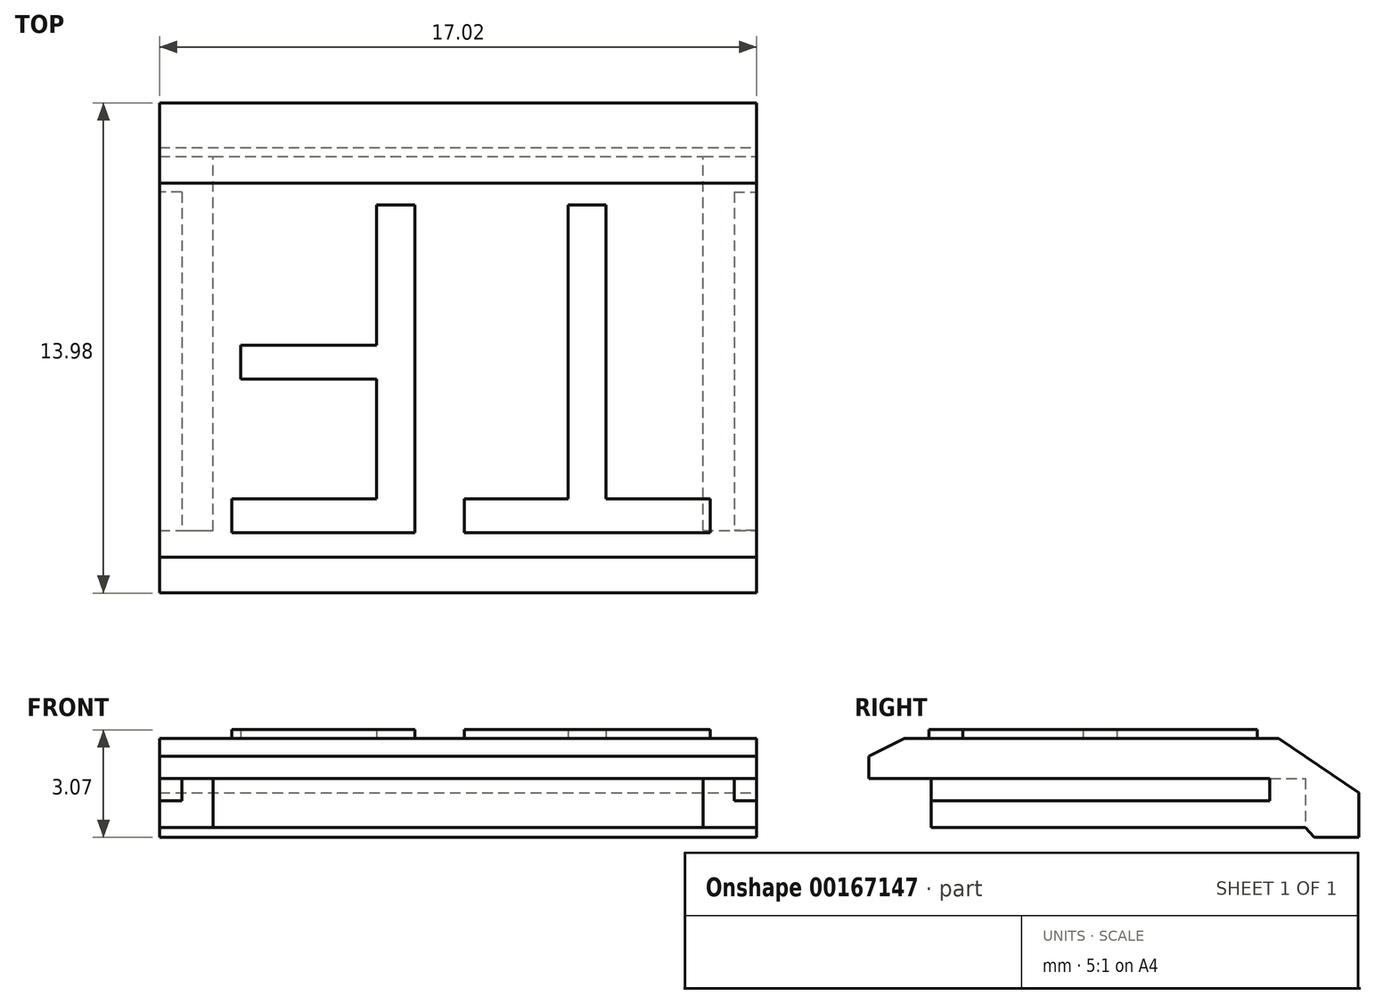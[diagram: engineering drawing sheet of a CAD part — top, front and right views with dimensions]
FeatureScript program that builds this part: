
annotation { "Feature Type Name" : "Feature", "Feature Type Description" : "" }
export const myFeature = defineFeature(function(context is Context, id is Id, definition is map)
    precondition{}
    {
        {
            var Q0;
            Q0=qCreatedBy(makeId("Top.planeOp"),FACE);
            var sketch = newSketch(context, id + "F0", { "sketchPlane" : qUnion([Q0])});
            skLineSegment(sketch, "E0.bottom", {"start": v(-8.5, 6.99) * mm, "end": v(8.5, 6.99) * mm});
            skLineSegment(sketch, "E0.top", {"start": v(-8.5, -6.99) * mm, "end": v(8.5, -6.99) * mm});
            skLineSegment(sketch, "E0.left", {"start": v(-8.5, 6.99) * mm, "end": v(-8.5, -6.99) * mm});
            skLineSegment(sketch, "E0.right", {"start": v(8.5, 6.99) * mm, "end": v(8.5, -6.99) * mm});
            skLineSegment(sketch, "E1", {"start": v(0, 0) * mm, "end": v(0, 6.99) * mm, "construction": true});
            skLineSegment(sketch, "E2", {"start": v(0, 0) * mm, "end": v(-8.5, 0) * mm, "construction": true});
            skSolve(sketch);
        }
        {
            var Q0;
            Q0=makeQuery(id+"F0.imprint","IMPRINT",FACE,{"disambiguationData":[TD([[makeQuery(id+"F0.imprint","IMPRINT",EDGE,{"derivedFrom":sQuery(id+"F0.wireOp",EDGE,"E0.bottom")}),-1.0]])]});
            extrude(context, id + "F1", {"entities" : qUnion([Q0]), "depth" : 2.54 * mm});
        }
        {
            var Q0;
            Q0=makeQuery(id+"F1.opExtrude","SWEPT_FACE",FACE,{"disambiguationData":[OSD([sQuery(id+"F0.wireOp",EDGE,"E0.right")])]});
            var sketch = newSketch(context, id + "F2", { "sketchPlane" : qUnion([Q0])});
            skLineSegment(sketch, "E3", {"start": v(6.99, 0) * mm, "end": v(6.99, -0.28) * mm});
            skLineSegment(sketch, "E4", {"start": v(6.99, -0.28) * mm, "end": v(5.72, -0.28) * mm});
            skLineSegment(sketch, "E5", {"start": v(5.72, -0.28) * mm, "end": v(5.46, 0) * mm});
            skSolve(sketch);
        }
        {
            var Q0;
            {var subQ0=sQuery(id+"F2.wireOp",EDGE,"E3");Q0=makeQuery(id+"F2.imprint","IMPRINT",FACE,{"disambiguationData":[TD([[makeQuery(id+"F2.imprint","IMPRINT",EDGE,{"derivedFrom":subQ0}),-1.0]])]});}
            var Q1;
            Q1=makeQuery(id+"F1.opExtrude","SWEPT_FACE",FACE,{"disambiguationData":[OSD([sQuery(id+"F0.wireOp",EDGE,"E0.left")])]});
            extrude(context, id + "F3", {"entities" : qUnion([Q0]), "operationType" : NewBodyOperationType.ADD, "endBound" : BoundingType.UP_TO_SURFACE, "oppositeDirection" : true, "endBoundEntityFace" : qUnion([Q1]), "depth" : 25.4 * mm});
        }
        {
            var Q0;
            {var subQ0=sQuery(id+"F0.wireOp",EDGE,"E0.right");Q0=makeQuery(id+"F3.boolean.opBoolean","MERGE",FACE,{"derivedFrom":[makeQuery(id+"F1.opExtrude","SWEPT_FACE",FACE,{"disambiguationData":[OSD([subQ0])]}),makeQuery(id+"F3.opExtrude","CAP_FACE",FACE,{"disambiguationData":[OSD([subQ0,sQuery(id+"F2.wireOp",EDGE,"E3"),sQuery(id+"F2.wireOp",EDGE,"E4"),sQuery(id+"F2.wireOp",EDGE,"E5")])],"isStart":true})]});}
            var sketch = newSketch(context, id + "F4", { "sketchPlane" : qUnion([Q0])});
            skLineSegment(sketch, "E6", {"start": v(4.7, 2.54) * mm, "end": v(6.99, 1) * mm});
            skSolve(sketch);
        }
        {
            var Q0;
            {var subQ0=sQuery(id+"F4.wireOp",EDGE,"E6");Q0=makeQuery(id+"F4.imprint","IMPRINT",FACE,{"disambiguationData":[TD([[makeQuery(id+"F4.imprint","IMPRINT",EDGE,{"derivedFrom":subQ0}),1.0]])]});}
            var Q1;
            {var subQ0=sQuery(id+"F0.wireOp",EDGE,"E0.left");Q1=makeQuery(id+"F3.boolean.opBoolean","MERGE",FACE,{"derivedFrom":[makeQuery(id+"F1.opExtrude","SWEPT_FACE",FACE,{"disambiguationData":[OSD([subQ0])]}),makeQuery(id+"F3.opExtrude","CAP_FACE",FACE,{"disambiguationData":[OSD([subQ0])],"isStart":false})]});}
            extrude(context, id + "F5", {"entities" : qUnion([Q0]), "operationType" : NewBodyOperationType.REMOVE, "endBound" : BoundingType.UP_TO_SURFACE, "oppositeDirection" : true, "endBoundEntityFace" : qUnion([Q1]), "depth" : 25.4 * mm});
        }
        {
            var Q0;
            Q0=makeQuery(id+"F1.opExtrude","SWEPT_FACE",FACE,{"disambiguationData":[OSD([sQuery(id+"F0.wireOp",EDGE,"E0.top")])]});
            var sketch = newSketch(context, id + "F6", { "sketchPlane" : qUnion([Q0])});
            skLineSegment(sketch, "E7.bottom", {"start": v(7.87, 1.4) * mm, "end": v(8.5, 1.4) * mm});
            skLineSegment(sketch, "E7.top", {"start": v(7.87, 0.76) * mm, "end": v(8.5, 0.76) * mm});
            skLineSegment(sketch, "E7.left", {"start": v(7.87, 1.4) * mm, "end": v(7.87, 0.76) * mm});
            skLineSegment(sketch, "E7.right", {"start": v(8.5, 1.4) * mm, "end": v(8.5, 0.76) * mm});
            skLineSegment(sketch, "E8", {"start": v(0, 0) * mm, "end": v(0, 2.54) * mm, "construction": true});
            skLineSegment(sketch, "E9.MirrorCS", {"start": v(-7.87, 0.76) * mm, "end": v(-8.5, 0.76) * mm});
            skLineSegment(sketch, "E10.MirrorCS", {"start": v(-7.87, 1.4) * mm, "end": v(-7.87, 0.76) * mm});
            skLineSegment(sketch, "E11.MirrorCS", {"start": v(-7.87, 1.4) * mm, "end": v(-8.5, 1.4) * mm});
            skLineSegment(sketch, "E12.MirrorCS", {"start": v(-8.5, 1.4) * mm, "end": v(-8.5, 0.76) * mm});
            skSolve(sketch);
        }
        {
            var Q0;
            Q0=makeQuery(id+"F6.imprint","IMPRINT",FACE,{"disambiguationData":[TD([[makeQuery(id+"F6.imprint","IMPRINT",EDGE,{"derivedFrom":sQuery(id+"F6.wireOp",EDGE,"E9.MirrorCS")}),-1.0]])]});
            var Q1;
            Q1=makeQuery(id+"F6.imprint","IMPRINT",FACE,{"disambiguationData":[TD([[makeQuery(id+"F6.imprint","IMPRINT",EDGE,{"derivedFrom":sQuery(id+"F6.wireOp",EDGE,"E7.bottom")}),-1.0]])]});
            extrude(context, id + "F7", {"entities" : qUnion([Q0, Q1]), "operationType" : NewBodyOperationType.REMOVE, "oppositeDirection" : true, "depth" : 11.43 * mm});
        }
        {
            var Q0;
            {var subQ0=sQuery(id+"F0.wireOp",EDGE,"E0.right");Q0=makeQuery(id+"F3.boolean.opBoolean","MERGE",FACE,{"derivedFrom":[makeQuery(id+"F1.opExtrude","SWEPT_FACE",FACE,{"disambiguationData":[OSD([subQ0])]}),makeQuery(id+"F3.opExtrude","CAP_FACE",FACE,{"disambiguationData":[OSD([subQ0,sQuery(id+"F2.wireOp",EDGE,"E3"),sQuery(id+"F2.wireOp",EDGE,"E4"),sQuery(id+"F2.wireOp",EDGE,"E5")])],"isStart":true})]});}
            var sketch = newSketch(context, id + "F8", { "sketchPlane" : qUnion([Q0])});
            skLineSegment(sketch, "E13.bottom", {"start": v(-6.98, 1.4) * mm, "end": v(-5.2, 1.4) * mm});
            skLineSegment(sketch, "E13.top", {"start": v(-6.98, 0) * mm, "end": v(-5.2, 0) * mm});
            skLineSegment(sketch, "E13.left", {"start": v(-6.98, 1.4) * mm, "end": v(-6.98, 0) * mm});
            skLineSegment(sketch, "E13.right", {"start": v(-5.2, 1.4) * mm, "end": v(-5.2, 0) * mm});
            skSolve(sketch);
        }
        {
            var Q0;
            {var subQ0=sQuery(id+"F8.wireOp",EDGE,"E13.bottom");Q0=makeQuery(id+"F8.imprint","IMPRINT",FACE,{"disambiguationData":[TD([[makeQuery(id+"F8.imprint","IMPRINT",EDGE,{"derivedFrom":subQ0}),1.0]])]});}
            var Q1;
            {var subQ0=sQuery(id+"F8.wireOp",EDGE,"E13.top");Q1=makeQuery(id+"F8.imprint","IMPRINT",FACE,{"disambiguationData":[TD([[makeQuery(id+"F8.imprint","IMPRINT",EDGE,{"derivedFrom":subQ0}),-1.0]])]});}
            var Q2;
            {var subQ0=sQuery(id+"F0.wireOp",EDGE,"E0.left");Q2=makeQuery(id+"F3.boolean.opBoolean","MERGE",FACE,{"derivedFrom":[makeQuery(id+"F1.opExtrude","SWEPT_FACE",FACE,{"disambiguationData":[OSD([subQ0])]}),makeQuery(id+"F3.opExtrude","CAP_FACE",FACE,{"disambiguationData":[OSD([subQ0])],"isStart":false})]});}
            extrude(context, id + "F9", {"entities" : qUnion([Q0, Q1]), "operationType" : NewBodyOperationType.REMOVE, "endBound" : BoundingType.UP_TO_SURFACE, "oppositeDirection" : true, "endBoundEntityFace" : qUnion([Q2]), "depth" : 25.4 * mm});
        }
        {
            var Q0;
            Q0=makeQuery(id+"F1.opExtrude","CAP_FACE",FACE,{"disambiguationData":[OSD([sQuery(id+"F0.wireOp",EDGE,"E0.bottom"),sQuery(id+"F0.wireOp",EDGE,"E0.top"),sQuery(id+"F0.wireOp",EDGE,"E0.left"),sQuery(id+"F0.wireOp",EDGE,"E0.right")])],"isStart":true});
            var sketch = newSketch(context, id + "F10", { "sketchPlane" : qUnion([Q0])});
            skLineSegment(sketch, "E14.bottom", {"start": v(-6.99, 5.2) * mm, "end": v(6.99, 5.2) * mm});
            skLineSegment(sketch, "E14.top", {"start": v(-6.99, -5.46) * mm, "end": v(6.99, -5.46) * mm});
            skLineSegment(sketch, "E14.left", {"start": v(-6.99, 5.2) * mm, "end": v(-6.99, -5.46) * mm});
            skLineSegment(sketch, "E14.right", {"start": v(6.99, 5.2) * mm, "end": v(6.99, -5.46) * mm});
            skLineSegment(sketch, "E15", {"start": v(6.99, -0.13) * mm, "end": v(8.5, -0.13) * mm, "construction": true});
            skLineSegment(sketch, "E16", {"start": v(-8.5, -0.13) * mm, "end": v(-6.99, -0.13) * mm, "construction": true});
            skSolve(sketch);
        }
        {
            var Q0;
            Q0=makeQuery(id+"F10.imprint","IMPRINT",FACE,{"disambiguationData":[TD([[makeQuery(id+"F10.imprint","IMPRINT",EDGE,{"derivedFrom":sQuery(id+"F10.wireOp",EDGE,"E14.bottom")}),-1.0]])]});
            var Q1;
            Q1=makeQuery(id+"F9.boolean.opBoolean","MERGE",FACE,{"derivedFrom":[makeQuery(id+"F7.boolean.opBoolean","COPY",FACE,{"derivedFrom":makeQuery(id+"F7.opExtrude","SWEPT_FACE",FACE,{"disambiguationData":[OSD([sQuery(id+"F6.wireOp",EDGE,"E7.bottom")])]})}),makeQuery(id+"F7.boolean.opBoolean","COPY",FACE,{"derivedFrom":makeQuery(id+"F7.opExtrude","SWEPT_FACE",FACE,{"disambiguationData":[OSD([sQuery(id+"F6.wireOp",EDGE,"E11.MirrorCS")])]})}),makeQuery(id+"F9.opExtrude","SWEPT_FACE",FACE,{"disambiguationData":[OSD([sQuery(id+"F8.wireOp",EDGE,"E13.bottom")])]})]});
            extrude(context, id + "F11", {"entities" : qUnion([Q0]), "operationType" : NewBodyOperationType.REMOVE, "endBound" : BoundingType.UP_TO_SURFACE, "oppositeDirection" : true, "endBoundEntityFace" : qUnion([Q1]), "depth" : 25.4 * mm});
        }
        {
            var Q0;
            {var subQ0=sQuery(id+"F0.wireOp",EDGE,"E0.right");Q0=makeQuery(id+"F3.boolean.opBoolean","MERGE",FACE,{"derivedFrom":[makeQuery(id+"F1.opExtrude","SWEPT_FACE",FACE,{"disambiguationData":[OSD([subQ0])]}),makeQuery(id+"F3.opExtrude","CAP_FACE",FACE,{"disambiguationData":[OSD([subQ0,sQuery(id+"F2.wireOp",EDGE,"E3"),sQuery(id+"F2.wireOp",EDGE,"E4"),sQuery(id+"F2.wireOp",EDGE,"E5")])],"isStart":true})]});}
            var sketch = newSketch(context, id + "F12", { "sketchPlane" : qUnion([Q0])});
            skLineSegment(sketch, "E17", {"start": v(-6.98, 2.03) * mm, "end": v(-5.97, 2.54) * mm});
            skLineSegment(sketch, "E18", {"start": v(-5.97, 2.54) * mm, "end": v(-6.98, 2.54) * mm, "construction": true});
            skLineSegment(sketch, "E19", {"start": v(-6.98, 2.54) * mm, "end": v(-6.98, 2.03) * mm, "construction": true});
            skSolve(sketch);
        }
        {
            var Q0;
            {var subQ0=sQuery(id+"F12.wireOp",EDGE,"E17");Q0=makeQuery(id+"F12.imprint","IMPRINT",FACE,{"disambiguationData":[TD([[makeQuery(id+"F12.imprint","IMPRINT",EDGE,{"derivedFrom":subQ0}),1.0]])]});}
            var Q1;
            {var subQ0=sQuery(id+"F0.wireOp",EDGE,"E0.left");Q1=makeQuery(id+"F3.boolean.opBoolean","MERGE",FACE,{"derivedFrom":[makeQuery(id+"F1.opExtrude","SWEPT_FACE",FACE,{"disambiguationData":[OSD([subQ0])]}),makeQuery(id+"F3.opExtrude","CAP_FACE",FACE,{"disambiguationData":[OSD([subQ0])],"isStart":false})]});}
            extrude(context, id + "F13", {"entities" : qUnion([Q0]), "operationType" : NewBodyOperationType.REMOVE, "endBound" : BoundingType.UP_TO_SURFACE, "oppositeDirection" : true, "endBoundEntityFace" : qUnion([Q1]), "depth" : 25.4 * mm});
        }
        {
            var Q0;
            Q0=makeQuery(id+"F1.opExtrude","CAP_FACE",FACE,{"disambiguationData":[OSD([sQuery(id+"F0.wireOp",EDGE,"E0.bottom"),sQuery(id+"F0.wireOp",EDGE,"E0.top"),sQuery(id+"F0.wireOp",EDGE,"E0.left"),sQuery(id+"F0.wireOp",EDGE,"E0.right")])],"isStart":false});
            var sketch = newSketch(context, id + "F14", { "sketchPlane" : qUnion([Q0])});
            skText(sketch, "E20", { "text": "TF", "fontName": "OpenSans-Regular.ttf"});
            skLineSegment(sketch, "E21", {"start": v(-7.3, -5.35) * mm, "end": v(-1.2, -11.44) * mm, "construction": true});
            skLineSegment(sketch, "E22", {"start": v(-7.3, -5.35) * mm, "end": v(13.6, -5.35) * mm, "construction": true});
            skLineSegment(sketch, "E23", {"start": v(0, -5.35) * mm, "end": v(0, -5.97) * mm, "construction": true});
            skLineSegment(sketch, "E24", {"start": v(0, 4.08) * mm, "end": v(0, 4.7) * mm, "construction": true});
            skLineSegment(sketch, "E25", {"start": v(-8.5, -0.63) * mm, "end": v(-7.3, -0.63) * mm, "construction": true});
            skLineSegment(sketch, "E26", {"start": v(7.3, -0.63) * mm, "end": v(8.5, -0.63) * mm, "construction": true});
            const initialGuessF14  = {"E20": [0.0073, 0.00408, -1, 0, 0.00943]};
            skSetInitialGuess(sketch, initialGuessF14);
            skSolve(sketch);
        }
        {
            var Q0;
            Q0=makeQuery(id+"F14.imprint","IMPRINT",FACE,{"disambiguationData":[TD([[makeQuery(id+"F14.imprint","IMPRINT",EDGE,{"derivedFrom":sQuery(id+"F14.wireOp",EDGE,"E20.sketch_text.stroke-8")}),-1.0]])]});
            var Q1;
            Q1=makeQuery(id+"F14.imprint","IMPRINT",FACE,{"disambiguationData":[TD([[makeQuery(id+"F14.imprint","IMPRINT",EDGE,{"derivedFrom":sQuery(id+"F14.wireOp",EDGE,"E20.sketch_text.stroke-0")}),-1.0]])]});
            extrude(context, id + "F15", {"entities" : qUnion([Q0, Q1]), "operationType" : NewBodyOperationType.ADD, "depth" : 0.25 * mm});
        }
    });
